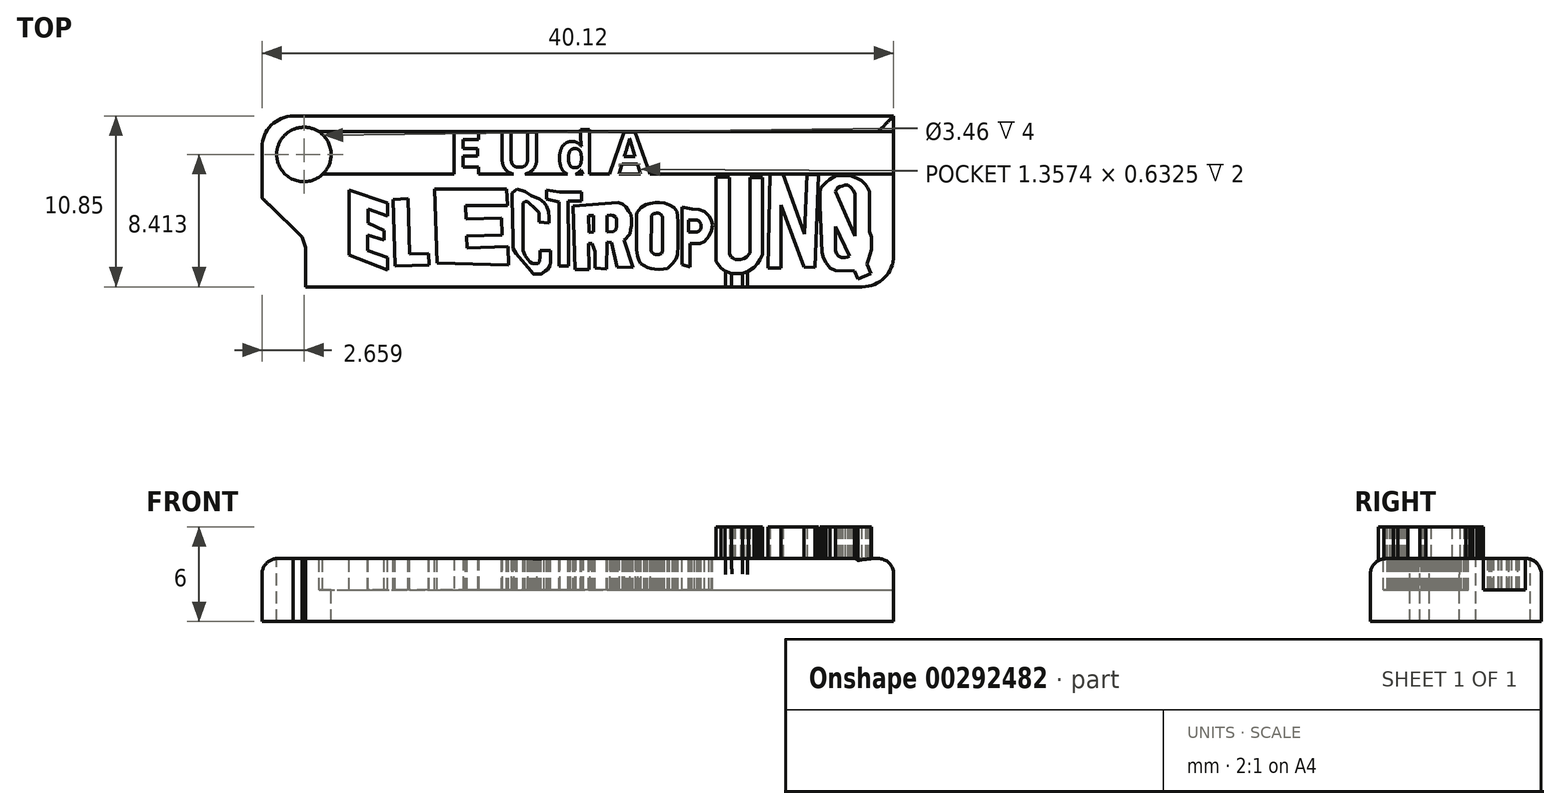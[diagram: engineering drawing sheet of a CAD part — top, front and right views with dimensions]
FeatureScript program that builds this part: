
annotation { "Feature Type Name" : "Feature", "Feature Type Description" : "" }
export const myFeature = defineFeature(function(context is Context, id is Id, definition is map)
    precondition{}
    {
        {
            var Q0;
            Q0=qCreatedBy(makeId("Top.planeOp"),FACE);
            var sketch = newSketch(context, id + "F0", { "sketchPlane" : qUnion([Q0])});
            skLineSegment(sketch, "E0.bottom", {"start": v(-20.57, 6.35) * mm, "end": v(19.55, 6.35) * mm});
            skLineSegment(sketch, "E0.top", {"start": v(-20.57, -4.5) * mm, "end": v(19.55, -4.5) * mm});
            skLineSegment(sketch, "E0.left", {"start": v(-20.57, 6.35) * mm, "end": v(-20.57, -4.5) * mm});
            skLineSegment(sketch, "E0.right", {"start": v(19.55, 6.35) * mm, "end": v(19.55, -4.5) * mm});
            skSolve(sketch);
        }
        {
            var Q0;
            Q0 = qSketchRegion(id + "F0", true);
            extrude(context, id + "F1", {"entities" : qUnion([Q0]), "oppositeDirection" : true, "depth" : 4 * mm});
        }
        {
            var Q0;
            Q0=makeQuery(id+"F1.opExtrude","CAP_FACE",FACE,{"disambiguationData":[OSD([sQuery(id+"F0.wireOp",EDGE,"E0.bottom"),sQuery(id+"F0.wireOp",EDGE,"E0.top"),sQuery(id+"F0.wireOp",EDGE,"E0.left"),sQuery(id+"F0.wireOp",EDGE,"E0.right")])],"isStart":true});
            var sketch = newSketch(context, id + "F2", { "sketchPlane" : qUnion([Q0])});
            skCircle(sketch, "E1", {"center": v(-17.91, 3.91) * mm, "radius": 1.73 * mm});
            skPoint(sketch, "E1.first.point", {"position": v(-19.2, 5.07) * mm});
            skPoint(sketch, "E1.second.point", {"position": v(-16.55, 2.84) * mm});
            skPoint(sketch, "E1.third.point", {"position": v(-16.4, 3.07) * mm});
            skSolve(sketch);
        }
        {
            var Q0;
            Q0=makeQuery(id+"F2.imprint","IMPRINT",FACE,{"disambiguationData":[TD([[makeQuery(id+"F2.imprint","IMPRINT",EDGE,{"derivedFrom":sQuery(id+"F2.wireOp",EDGE,"E1")}),1.0]])]});
            extrude(context, id + "F3", {"entities" : qUnion([Q0]), "operationType" : NewBodyOperationType.REMOVE, "oppositeDirection" : true, "depth" : 25 * mm});
        }
        {
            var Q0;
            Q0=qCreatedBy(makeId("Top.planeOp"),FACE);
            var sketch = newSketch(context, id + "F4", { "sketchPlane" : qUnion([Q0])});
            skLineSegment(sketch, "E2", {"start": v(-12.6, 0.81) * mm, "end": v(-12.6, 0) * mm});
            skLineSegment(sketch, "E3", {"start": v(-12.6, 0) * mm, "end": v(-13.83, 0.46) * mm});
            skLineSegment(sketch, "E4", {"start": v(-13.83, 0.46) * mm, "end": v(-13.83, -0.46) * mm});
            skLineSegment(sketch, "E5", {"start": v(-13.83, -0.46) * mm, "end": v(-12.8, -0.92) * mm});
            skLineSegment(sketch, "E6", {"start": v(-12.8, -0.92) * mm, "end": v(-12.8, -1.52) * mm});
            skLineSegment(sketch, "E7", {"start": v(-12.8, -1.52) * mm, "end": v(-13.87, -1.2) * mm});
            skLineSegment(sketch, "E8", {"start": v(-13.87, -1.2) * mm, "end": v(-13.87, -2.2) * mm});
            skLineSegment(sketch, "E9", {"start": v(-13.87, -2.2) * mm, "end": v(-12.6, -2.65) * mm});
            skLineSegment(sketch, "E10", {"start": v(-12.6, -2.65) * mm, "end": v(-12.6, -3.43) * mm});
            skLineSegment(sketch, "E11", {"start": v(-12.6, -3.43) * mm, "end": v(-15.03, -2.47) * mm});
            skLineSegment(sketch, "E12", {"start": v(-15.03, -2.47) * mm, "end": v(-15.03, 1.66) * mm});
            skLineSegment(sketch, "E13", {"start": v(-15.03, 1.66) * mm, "end": v(-12.6, 0.81) * mm});
            skLineSegment(sketch, "E14", {"start": v(-12.25, 1.06) * mm, "end": v(-12.1, -3.17) * mm});
            skLineSegment(sketch, "E15", {"start": v(-12.1, -3.17) * mm, "end": v(-9.96, -3.1) * mm});
            skLineSegment(sketch, "E16", {"start": v(-9.96, -3.1) * mm, "end": v(-9.99, -2.37) * mm});
            skLineSegment(sketch, "E17", {"start": v(-9.99, -2.37) * mm, "end": v(-11.19, -2.4) * mm});
            skLineSegment(sketch, "E18", {"start": v(-11.19, -2.4) * mm, "end": v(-11.3, 1.11) * mm});
            skLineSegment(sketch, "E19", {"start": v(-11.3, 1.11) * mm, "end": v(-12.25, 1.06) * mm});
            skLineSegment(sketch, "E20", {"start": v(-5, 0.65) * mm, "end": v(-5.03, 1.7) * mm});
            skLineSegment(sketch, "E21", {"start": v(-5.03, 1.7) * mm, "end": v(-9.6, 1.7) * mm});
            skLineSegment(sketch, "E22", {"start": v(-9.6, 1.7) * mm, "end": v(-9.45, -2.98) * mm});
            skLineSegment(sketch, "E23", {"start": v(-9.45, -2.98) * mm, "end": v(-4.91, -3.1) * mm});
            skLineSegment(sketch, "E24", {"start": v(-4.91, -3.1) * mm, "end": v(-4.95, -1.94) * mm});
            skLineSegment(sketch, "E25", {"start": v(-4.95, -1.94) * mm, "end": v(-7.54, -2.03) * mm});
            skLineSegment(sketch, "E26", {"start": v(-7.54, -2.03) * mm, "end": v(-7.56, -1.27) * mm});
            skLineSegment(sketch, "E27", {"start": v(-7.56, -1.27) * mm, "end": v(-5.32, -1.19) * mm});
            skLineSegment(sketch, "E28", {"start": v(-5.32, -1.19) * mm, "end": v(-5.36, -0.12) * mm});
            skLineSegment(sketch, "E29", {"start": v(-5.36, -0.12) * mm, "end": v(-7.6, -0.2) * mm});
            skLineSegment(sketch, "E30", {"start": v(-7.6, -0.2) * mm, "end": v(-7.63, 0.65) * mm});
            skLineSegment(sketch, "E31", {"start": v(-7.63, 0.65) * mm, "end": v(-5, 0.65) * mm});
            skLineSegment(sketch, "E32", {"start": v(-2.91, -2.17) * mm, "end": v(-2.24, -2.17) * mm});
            skLineSegment(sketch, "E33", {"start": v(-2.24, -2.17) * mm, "end": v(-2.24, -2.93) * mm});
            skLineSegment(sketch, "E34", {"start": v(-2.24, -2.93) * mm, "end": v(-2.28, -3.15) * mm});
            skLineSegment(sketch, "E35", {"start": v(-2.28, -3.15) * mm, "end": v(-2.44, -3.4) * mm});
            skLineSegment(sketch, "E36", {"start": v(-2.44, -3.4) * mm, "end": v(-2.84, -3.7) * mm});
            skLineSegment(sketch, "E37", {"start": v(-2.84, -3.7) * mm, "end": v(-2.95, -3.7) * mm});
            skLineSegment(sketch, "E38", {"start": v(-3.34, -3.7) * mm, "end": v(-2.95, -3.7) * mm});
            skLineSegment(sketch, "E39", {"start": v(-3.34, -3.7) * mm, "end": v(-4.43, -2.39) * mm});
            skLineSegment(sketch, "E40", {"start": v(-4.43, -2.39) * mm, "end": v(-4.63, -2.05) * mm});
            skLineSegment(sketch, "E41", {"start": v(-4.63, -2.05) * mm, "end": v(-4.63, -1.47) * mm});
            skLineSegment(sketch, "E42", {"start": v(-4.63, -1.47) * mm, "end": v(-4.7, 1.16) * mm});
            skLineSegment(sketch, "E43", {"start": v(-4.7, 1.16) * mm, "end": v(-4.7, 1.45) * mm});
            skLineSegment(sketch, "E44", {"start": v(-4.7, 1.45) * mm, "end": v(-4.38, 1.71) * mm});
            skLineSegment(sketch, "E45", {"start": v(-4.38, 1.71) * mm, "end": v(-3.87, 1.55) * mm});
            skLineSegment(sketch, "E46", {"start": v(-3.87, 1.55) * mm, "end": v(-3.5, 1.29) * mm});
            skLineSegment(sketch, "E47", {"start": v(-3.5, 1.29) * mm, "end": v(-2.95, 1.1) * mm});
            skLineSegment(sketch, "E48", {"start": v(-2.95, 1.1) * mm, "end": v(-2.65, 0.85) * mm});
            skLineSegment(sketch, "E49", {"start": v(-2.65, 0.85) * mm, "end": v(-2.49, 0.63) * mm});
            skLineSegment(sketch, "E50", {"start": v(-2.49, 0.63) * mm, "end": v(-2.36, 0.3) * mm});
            skLineSegment(sketch, "E51", {"start": v(-2.36, 0.3) * mm, "end": v(-2.33, -0.1) * mm});
            skLineSegment(sketch, "E52", {"start": v(-2.33, -0.1) * mm, "end": v(-2.33, -0.44) * mm});
            skLineSegment(sketch, "E53", {"start": v(-2.33, -0.44) * mm, "end": v(-2.98, -0.37) * mm});
            skLineSegment(sketch, "E54", {"start": v(-2.98, -0.37) * mm, "end": v(-2.98, 0.21) * mm});
            skLineSegment(sketch, "E55", {"start": v(-2.98, 0.21) * mm, "end": v(-3.18, 0.42) * mm});
            skLineSegment(sketch, "E56", {"start": v(-3.18, 0.42) * mm, "end": v(-3.7, 0.92) * mm});
            skLineSegment(sketch, "E57", {"start": v(-3.7, 0.92) * mm, "end": v(-3.87, 0.92) * mm});
            skLineSegment(sketch, "E58", {"start": v(-3.87, 0.92) * mm, "end": v(-3.98, 0.83) * mm});
            skLineSegment(sketch, "E59", {"start": v(-3.98, 0.83) * mm, "end": v(-3.98, 0.56) * mm});
            skLineSegment(sketch, "E60", {"start": v(-3.98, 0.56) * mm, "end": v(-3.98, -0.87) * mm});
            skLineSegment(sketch, "E61", {"start": v(-3.98, -0.87) * mm, "end": v(-3.98, -1.91) * mm});
            skLineSegment(sketch, "E62", {"start": v(-3.98, -1.91) * mm, "end": v(-3.98, -2.17) * mm});
            skLineSegment(sketch, "E63", {"start": v(-3.98, -2.17) * mm, "end": v(-3.87, -2.5) * mm});
            skLineSegment(sketch, "E64", {"start": v(-3.87, -2.5) * mm, "end": v(-3.7, -2.73) * mm});
            skLineSegment(sketch, "E65", {"start": v(-3.7, -2.73) * mm, "end": v(-3.54, -2.91) * mm});
            skLineSegment(sketch, "E66", {"start": v(-3.54, -2.91) * mm, "end": v(-3.4, -3) * mm});
            skLineSegment(sketch, "E67", {"start": v(-3.4, -3) * mm, "end": v(-3.18, -3) * mm});
            skLineSegment(sketch, "E68", {"start": v(-3.18, -3) * mm, "end": v(-3.05, -3) * mm});
            skLineSegment(sketch, "E69", {"start": v(-3.05, -3) * mm, "end": v(-2.95, -2.88) * mm});
            skLineSegment(sketch, "E70", {"start": v(-2.95, -2.88) * mm, "end": v(-2.9, -2.58) * mm});
            skLineSegment(sketch, "E71", {"start": v(-2.9, -2.58) * mm, "end": v(-2.91, -2.17) * mm});
            skLineSegment(sketch, "E72", {"start": v(-2.5, 1.09) * mm, "end": v(-2.5, 1.64) * mm});
            skLineSegment(sketch, "E73", {"start": v(-2.5, 1.64) * mm, "end": v(-1.68, 1.51) * mm});
            skLineSegment(sketch, "E74", {"start": v(-1.68, 1.51) * mm, "end": v(-0.27, 1.51) * mm});
            skLineSegment(sketch, "E75", {"start": v(-0.27, 1.51) * mm, "end": v(-0.27, 0.96) * mm});
            skLineSegment(sketch, "E76", {"start": v(-0.27, 0.96) * mm, "end": v(-1.13, 0.96) * mm});
            skLineSegment(sketch, "E77", {"start": v(-1.13, 0.96) * mm, "end": v(-1.12, -1.93) * mm});
            skLineSegment(sketch, "E78", {"start": v(-1.12, -1.93) * mm, "end": v(-1.12, -3.19) * mm});
            skLineSegment(sketch, "E79", {"start": v(-1.12, -3.19) * mm, "end": v(-1.71, -3.19) * mm});
            skLineSegment(sketch, "E80", {"start": v(-1.71, -3.19) * mm, "end": v(-1.71, -1.63) * mm});
            skLineSegment(sketch, "E81", {"start": v(-1.71, -1.63) * mm, "end": v(-1.71, 0.9) * mm});
            skLineSegment(sketch, "E82", {"start": v(-1.71, 0.9) * mm, "end": v(-2.5, 1.09) * mm});
            skLineSegment(sketch, "E83", {"start": v(-0.7, -3.39) * mm, "end": v(-0.82, 0.63) * mm});
            skLineSegment(sketch, "E84", {"start": v(-0.82, 0.63) * mm, "end": v(2.04, 0.84) * mm});
            skLineSegment(sketch, "E85", {"start": v(2.04, 0.84) * mm, "end": v(2.33, 0.77) * mm});
            skLineSegment(sketch, "E86", {"start": v(2.33, 0.77) * mm, "end": v(2.54, 0.58) * mm});
            skLineSegment(sketch, "E87", {"start": v(2.54, 0.58) * mm, "end": v(2.72, 0.3) * mm});
            skLineSegment(sketch, "E88", {"start": v(2.72, 0.3) * mm, "end": v(2.87, 0.08) * mm});
            skLineSegment(sketch, "E89", {"start": v(2.87, 0.08) * mm, "end": v(2.9, -0.2) * mm});
            skLineSegment(sketch, "E90", {"start": v(2.9, -0.2) * mm, "end": v(2.9, -0.6) * mm});
            skLineSegment(sketch, "E91", {"start": v(2.9, -0.6) * mm, "end": v(2.84, -0.86) * mm});
            skLineSegment(sketch, "E92", {"start": v(2.84, -0.86) * mm, "end": v(2.8, -1.13) * mm});
            skLineSegment(sketch, "E93", {"start": v(2.8, -1.13) * mm, "end": v(2.67, -1.28) * mm});
            skLineSegment(sketch, "E94", {"start": v(2.67, -1.28) * mm, "end": v(2.56, -1.43) * mm});
            skLineSegment(sketch, "E95", {"start": v(2.56, -1.43) * mm, "end": v(2.43, -1.52) * mm});
            skLineSegment(sketch, "E96", {"start": v(2.43, -1.52) * mm, "end": v(3, -3.27) * mm});
            skLineSegment(sketch, "E97", {"start": v(3, -3.27) * mm, "end": v(1.98, -3.23) * mm});
            skLineSegment(sketch, "E98", {"start": v(1.98, -3.23) * mm, "end": v(1.62, -1.67) * mm});
            skLineSegment(sketch, "E99", {"start": v(1.62, -1.67) * mm, "end": v(1.35, -1.65) * mm});
            skLineSegment(sketch, "E100", {"start": v(1.35, -1.65) * mm, "end": v(1.33, -3.35) * mm});
            skLineSegment(sketch, "E101", {"start": v(1.33, -3.35) * mm, "end": v(0.6, -3.31) * mm});
            skLineSegment(sketch, "E102", {"start": v(0.6, -3.31) * mm, "end": v(0.57, -2.24) * mm});
            skLineSegment(sketch, "E103", {"start": v(0.57, -2.24) * mm, "end": v(0.38, -1.74) * mm});
            skLineSegment(sketch, "E104", {"start": v(0.38, -1.74) * mm, "end": v(0.17, -1.74) * mm});
            skLineSegment(sketch, "E105", {"start": v(0.17, -1.74) * mm, "end": v(0.2, -3.4) * mm});
            skLineSegment(sketch, "E106", {"start": v(0.2, -3.4) * mm, "end": v(-0.7, -3.39) * mm});
            skLineSegment(sketch, "E107", {"start": v(0.48, -1.02) * mm, "end": v(0.18, -1.03) * mm});
            skLineSegment(sketch, "E108", {"start": v(0.18, -1.03) * mm, "end": v(0.18, 0.04) * mm});
            skLineSegment(sketch, "E109", {"start": v(0.18, 0.04) * mm, "end": v(0.48, 0.04) * mm});
            skLineSegment(sketch, "E110", {"start": v(0.48, 0.04) * mm, "end": v(0.48, -1.02) * mm});
            skLineSegment(sketch, "E111", {"start": v(1.34, 0.04) * mm, "end": v(1.34, -1.02) * mm});
            skLineSegment(sketch, "E112", {"start": v(1.34, -1.02) * mm, "end": v(1.74, -1) * mm});
            skLineSegment(sketch, "E113", {"start": v(1.74, -1) * mm, "end": v(1.9, -0.85) * mm});
            skLineSegment(sketch, "E114", {"start": v(1.9, -0.85) * mm, "end": v(1.96, -0.64) * mm});
            skLineSegment(sketch, "E115", {"start": v(1.96, -0.64) * mm, "end": v(1.95, -0.38) * mm});
            skLineSegment(sketch, "E116", {"start": v(1.95, -0.38) * mm, "end": v(1.93, -0.2) * mm});
            skLineSegment(sketch, "E117", {"start": v(1.93, -0.2) * mm, "end": v(1.87, -0.05) * mm});
            skLineSegment(sketch, "E118", {"start": v(1.87, -0.05) * mm, "end": v(1.73, 0.03) * mm});
            skLineSegment(sketch, "E119", {"start": v(1.73, 0.03) * mm, "end": v(1.56, 0.05) * mm});
            skLineSegment(sketch, "E120", {"start": v(1.56, 0.05) * mm, "end": v(1.38, 0.04) * mm});
            skLineSegment(sketch, "E121", {"start": v(1.38, 0.04) * mm, "end": v(1.34, 0.04) * mm});
            skLineSegment(sketch, "E122", {"start": v(3.23, 0) * mm, "end": v(3.23, -2.14) * mm});
            skLineSegment(sketch, "E123", {"start": v(3.23, -2.14) * mm, "end": v(3.27, -2.55) * mm});
            skLineSegment(sketch, "E124", {"start": v(3.27, -2.55) * mm, "end": v(3.38, -2.81) * mm});
            skLineSegment(sketch, "E125", {"start": v(3.38, -2.81) * mm, "end": v(3.45, -3.02) * mm});
            skLineSegment(sketch, "E126", {"start": v(3.45, -3.02) * mm, "end": v(3.68, -3.15) * mm});
            skLineSegment(sketch, "E127", {"start": v(3.68, -3.15) * mm, "end": v(3.92, -3.28) * mm});
            skLineSegment(sketch, "E128", {"start": v(3.92, -3.28) * mm, "end": v(4.13, -3.32) * mm});
            skLineSegment(sketch, "E129", {"start": v(4.13, -3.32) * mm, "end": v(4.37, -3.36) * mm});
            skLineSegment(sketch, "E130", {"start": v(4.37, -3.36) * mm, "end": v(4.63, -3.4) * mm});
            skLineSegment(sketch, "E131", {"start": v(4.63, -3.4) * mm, "end": v(4.93, -3.36) * mm});
            skLineSegment(sketch, "E132", {"start": v(4.93, -3.36) * mm, "end": v(5.2, -3.32) * mm});
            skLineSegment(sketch, "E133", {"start": v(5.2, -3.32) * mm, "end": v(5.5, -3.02) * mm});
            skLineSegment(sketch, "E134", {"start": v(5.5, -3.02) * mm, "end": v(5.72, -2.74) * mm});
            skLineSegment(sketch, "E135", {"start": v(5.72, -2.74) * mm, "end": v(5.81, -2.44) * mm});
            skLineSegment(sketch, "E136", {"start": v(5.81, -2.44) * mm, "end": v(5.85, -1.86) * mm});
            skLineSegment(sketch, "E137", {"start": v(5.85, -1.86) * mm, "end": v(5.85, -1.13) * mm});
            skLineSegment(sketch, "E138", {"start": v(5.85, -1.13) * mm, "end": v(5.85, -0.38) * mm});
            skLineSegment(sketch, "E139", {"start": v(5.85, -0.38) * mm, "end": v(5.83, 0.01) * mm});
            skLineSegment(sketch, "E140", {"start": v(5.83, 0.01) * mm, "end": v(5.77, 0.3) * mm});
            skLineSegment(sketch, "E141", {"start": v(5.77, 0.3) * mm, "end": v(5.6, 0.53) * mm});
            skLineSegment(sketch, "E142", {"start": v(5.6, 0.53) * mm, "end": v(5.32, 0.7) * mm});
            skLineSegment(sketch, "E143", {"start": v(5.32, 0.7) * mm, "end": v(5, 0.82) * mm});
            skLineSegment(sketch, "E144", {"start": v(5, 0.82) * mm, "end": v(4.69, 0.85) * mm});
            skLineSegment(sketch, "E145", {"start": v(4.69, 0.85) * mm, "end": v(4.4, 0.85) * mm});
            skLineSegment(sketch, "E146", {"start": v(4.4, 0.85) * mm, "end": v(4.07, 0.8) * mm});
            skLineSegment(sketch, "E147", {"start": v(4.07, 0.8) * mm, "end": v(3.8, 0.72) * mm});
            skLineSegment(sketch, "E148", {"start": v(3.8, 0.72) * mm, "end": v(3.5, 0.55) * mm});
            skLineSegment(sketch, "E149", {"start": v(3.5, 0.55) * mm, "end": v(3.34, 0.35) * mm});
            skLineSegment(sketch, "E150", {"start": v(3.34, 0.35) * mm, "end": v(3.25, 0.22) * mm});
            skLineSegment(sketch, "E151", {"start": v(3.25, 0.22) * mm, "end": v(3.22, 0.1) * mm});
            skLineSegment(sketch, "E152", {"start": v(3.22, 0.1) * mm, "end": v(3.23, 0) * mm});
            skLineSegment(sketch, "E153", {"start": v(4.16, -0.04) * mm, "end": v(4.14, -2.2) * mm});
            skLineSegment(sketch, "E154", {"start": v(4.14, -2.2) * mm, "end": v(4.2, -2.3) * mm});
            skLineSegment(sketch, "E155", {"start": v(4.2, -2.3) * mm, "end": v(4.28, -2.37) * mm});
            skLineSegment(sketch, "E156", {"start": v(4.28, -2.37) * mm, "end": v(4.34, -2.42) * mm});
            skLineSegment(sketch, "E157", {"start": v(4.34, -2.42) * mm, "end": v(4.43, -2.43) * mm});
            skLineSegment(sketch, "E158", {"start": v(4.43, -2.43) * mm, "end": v(4.53, -2.45) * mm});
            skLineSegment(sketch, "E159", {"start": v(4.53, -2.45) * mm, "end": v(4.64, -2.44) * mm});
            skLineSegment(sketch, "E160", {"start": v(4.64, -2.44) * mm, "end": v(4.71, -2.42) * mm});
            skLineSegment(sketch, "E161", {"start": v(4.71, -2.42) * mm, "end": v(4.8, -2.38) * mm});
            skLineSegment(sketch, "E162", {"start": v(4.8, -2.38) * mm, "end": v(4.84, -2.3) * mm});
            skLineSegment(sketch, "E163", {"start": v(4.84, -2.3) * mm, "end": v(4.87, -2.18) * mm});
            skLineSegment(sketch, "E164", {"start": v(4.87, -2.18) * mm, "end": v(4.87, -0.06) * mm});
            skLineSegment(sketch, "E165", {"start": v(4.87, -0.06) * mm, "end": v(4.84, 0.01) * mm});
            skLineSegment(sketch, "E166", {"start": v(4.84, 0.01) * mm, "end": v(4.78, 0.1) * mm});
            skLineSegment(sketch, "E167", {"start": v(4.78, 0.1) * mm, "end": v(4.67, 0.14) * mm});
            skLineSegment(sketch, "E168", {"start": v(4.67, 0.14) * mm, "end": v(4.57, 0.18) * mm});
            skLineSegment(sketch, "E169", {"start": v(4.57, 0.18) * mm, "end": v(4.47, 0.18) * mm});
            skLineSegment(sketch, "E170", {"start": v(4.47, 0.18) * mm, "end": v(4.39, 0.16) * mm});
            skLineSegment(sketch, "E171", {"start": v(4.39, 0.16) * mm, "end": v(4.3, 0.14) * mm});
            skLineSegment(sketch, "E172", {"start": v(4.3, 0.14) * mm, "end": v(4.22, 0.08) * mm});
            skLineSegment(sketch, "E173", {"start": v(4.22, 0.08) * mm, "end": v(4.16, 0.04) * mm});
            skLineSegment(sketch, "E174", {"start": v(4.16, 0.04) * mm, "end": v(4.16, -0.04) * mm});
            skLineSegment(sketch, "E175", {"start": v(6.12, 0.58) * mm, "end": v(6.12, -3.1) * mm});
            skLineSegment(sketch, "E176", {"start": v(6.12, -3.1) * mm, "end": v(6.61, -3.22) * mm});
            skLineSegment(sketch, "E177", {"start": v(6.61, -3.22) * mm, "end": v(6.61, -1.73) * mm});
            skLineSegment(sketch, "E178", {"start": v(6.61, -1.73) * mm, "end": v(7.25, -1.74) * mm});
            skLineSegment(sketch, "E179", {"start": v(7.25, -1.74) * mm, "end": v(7.53, -1.62) * mm});
            skLineSegment(sketch, "E180", {"start": v(7.53, -1.62) * mm, "end": v(7.83, -1.28) * mm});
            skLineSegment(sketch, "E181", {"start": v(7.83, -1.28) * mm, "end": v(7.98, -0.93) * mm});
            skLineSegment(sketch, "E182", {"start": v(7.98, -0.93) * mm, "end": v(8.04, -0.57) * mm});
            skLineSegment(sketch, "E183", {"start": v(8.04, -0.57) * mm, "end": v(7.98, -0.27) * mm});
            skLineSegment(sketch, "E184", {"start": v(7.98, -0.27) * mm, "end": v(7.82, 0) * mm});
            skLineSegment(sketch, "E185", {"start": v(7.82, 0) * mm, "end": v(7.53, 0.27) * mm});
            skLineSegment(sketch, "E186", {"start": v(7.53, 0.27) * mm, "end": v(7.18, 0.4) * mm});
            skLineSegment(sketch, "E187", {"start": v(7.18, 0.4) * mm, "end": v(6.74, 0.46) * mm});
            skLineSegment(sketch, "E188", {"start": v(6.74, 0.46) * mm, "end": v(6.12, 0.58) * mm});
            skLineSegment(sketch, "E189", {"start": v(6.53, -0.25) * mm, "end": v(6.53, -1) * mm});
            skLineSegment(sketch, "E190", {"start": v(6.53, -1) * mm, "end": v(7.07, -1.01) * mm});
            skLineSegment(sketch, "E191", {"start": v(7.07, -1.01) * mm, "end": v(7.18, -0.95) * mm});
            skLineSegment(sketch, "E192", {"start": v(7.18, -0.95) * mm, "end": v(7.28, -0.85) * mm});
            skLineSegment(sketch, "E193", {"start": v(7.28, -0.85) * mm, "end": v(7.3, -0.72) * mm});
            skLineSegment(sketch, "E194", {"start": v(7.3, -0.72) * mm, "end": v(7.32, -0.6) * mm});
            skLineSegment(sketch, "E195", {"start": v(7.32, -0.6) * mm, "end": v(7.3, -0.5) * mm});
            skLineSegment(sketch, "E196", {"start": v(7.3, -0.5) * mm, "end": v(7.25, -0.41) * mm});
            skLineSegment(sketch, "E197", {"start": v(7.25, -0.41) * mm, "end": v(7.17, -0.33) * mm});
            skLineSegment(sketch, "E198", {"start": v(7.17, -0.33) * mm, "end": v(7.06, -0.26) * mm});
            skLineSegment(sketch, "E199", {"start": v(7.06, -0.26) * mm, "end": v(6.91, -0.26) * mm});
            skLineSegment(sketch, "E200", {"start": v(6.91, -0.26) * mm, "end": v(6.53, -0.25) * mm});
            skSolve(sketch);
        }
        {
            var Q0;
            Q0=makeQuery(id+"F1.opExtrude","CAP_FACE",FACE,{"disambiguationData":[OSD([sQuery(id+"F0.wireOp",EDGE,"E0.bottom"),sQuery(id+"F0.wireOp",EDGE,"E0.top"),sQuery(id+"F0.wireOp",EDGE,"E0.left"),sQuery(id+"F0.wireOp",EDGE,"E0.right")])],"isStart":true});
            var sketch = newSketch(context, id + "F5", { "sketchPlane" : qUnion([Q0])});
            skLineSegment(sketch, "E201", {"start": v(8.25, 2.48) * mm, "end": v(8.25, -2.53) * mm});
            skLineSegment(sketch, "E202", {"start": v(8.25, -2.53) * mm, "end": v(8.25, -2.9) * mm});
            skLineSegment(sketch, "E203", {"start": v(8.25, -2.9) * mm, "end": v(8.57, -3.29) * mm});
            skLineSegment(sketch, "E204", {"start": v(8.57, -3.29) * mm, "end": v(8.83, -3.48) * mm});
            skLineSegment(sketch, "E205", {"start": v(8.83, -3.48) * mm, "end": v(9.25, -3.64) * mm});
            skLineSegment(sketch, "E206", {"start": v(9.25, -3.64) * mm, "end": v(9.58, -3.64) * mm});
            skLineSegment(sketch, "E207", {"start": v(9.58, -3.64) * mm, "end": v(9.96, -3.64) * mm});
            skLineSegment(sketch, "E208", {"start": v(9.96, -3.64) * mm, "end": v(10.32, -3.48) * mm});
            skLineSegment(sketch, "E209", {"start": v(10.32, -3.48) * mm, "end": v(10.67, -3.27) * mm});
            skLineSegment(sketch, "E210", {"start": v(10.67, -3.27) * mm, "end": v(10.9, -3.03) * mm});
            skLineSegment(sketch, "E211", {"start": v(10.9, -3.03) * mm, "end": v(11.07, -2.75) * mm});
            skLineSegment(sketch, "E212", {"start": v(11.07, -2.75) * mm, "end": v(11.2, -2.45) * mm});
            skLineSegment(sketch, "E213", {"start": v(11.2, -2.45) * mm, "end": v(11.2, 2.44) * mm});
            skLineSegment(sketch, "E214", {"start": v(11.2, 2.44) * mm, "end": v(10.44, 2.44) * mm});
            skLineSegment(sketch, "E215", {"start": v(10.44, 2.44) * mm, "end": v(10.44, -2.08) * mm});
            skLineSegment(sketch, "E216", {"start": v(10.44, -2.08) * mm, "end": v(10.44, -2.33) * mm});
            skLineSegment(sketch, "E217", {"start": v(10.44, -2.33) * mm, "end": v(10.2, -2.6) * mm});
            skLineSegment(sketch, "E218", {"start": v(10.2, -2.6) * mm, "end": v(10.05, -2.7) * mm});
            skLineSegment(sketch, "E219", {"start": v(10.05, -2.7) * mm, "end": v(9.84, -2.75) * mm});
            skLineSegment(sketch, "E220", {"start": v(9.84, -2.75) * mm, "end": v(9.66, -2.75) * mm});
            skLineSegment(sketch, "E221", {"start": v(9.66, -2.75) * mm, "end": v(9.47, -2.75) * mm});
            skLineSegment(sketch, "E222", {"start": v(9.47, -2.75) * mm, "end": v(9.33, -2.68) * mm});
            skLineSegment(sketch, "E223", {"start": v(9.33, -2.68) * mm, "end": v(9.22, -2.6) * mm});
            skLineSegment(sketch, "E224", {"start": v(9.22, -2.6) * mm, "end": v(9.11, -2.4) * mm});
            skLineSegment(sketch, "E225", {"start": v(9.11, -2.4) * mm, "end": v(9.11, 2.43) * mm});
            skLineSegment(sketch, "E226", {"start": v(9.11, 2.43) * mm, "end": v(8.25, 2.48) * mm});
            skLineSegment(sketch, "E227", {"start": v(11.57, -3.31) * mm, "end": v(11.7, 2.68) * mm});
            skLineSegment(sketch, "E228", {"start": v(11.7, 2.68) * mm, "end": v(12.51, 2.66) * mm});
            skLineSegment(sketch, "E229", {"start": v(12.51, 2.66) * mm, "end": v(13.9, -1.15) * mm});
            skLineSegment(sketch, "E230", {"start": v(13.9, -1.15) * mm, "end": v(14.03, 2.63) * mm});
            skLineSegment(sketch, "E231", {"start": v(14.03, 2.63) * mm, "end": v(14.77, 2.6) * mm});
            skLineSegment(sketch, "E232", {"start": v(14.77, 2.6) * mm, "end": v(14.55, -3.27) * mm});
            skLineSegment(sketch, "E233", {"start": v(14.55, -3.27) * mm, "end": v(13.84, -3.25) * mm});
            skLineSegment(sketch, "E234", {"start": v(13.84, -3.25) * mm, "end": v(12.39, 0.68) * mm});
            skLineSegment(sketch, "E235", {"start": v(12.39, 0.68) * mm, "end": v(12.39, -3.3) * mm});
            skLineSegment(sketch, "E236", {"start": v(12.39, -3.3) * mm, "end": v(11.57, -3.31) * mm});
            skLineSegment(sketch, "E237", {"start": v(14.93, 1.8) * mm, "end": v(14.88, 1.57) * mm});
            skLineSegment(sketch, "E238", {"start": v(14.88, 1.57) * mm, "end": v(14.88, 1.08) * mm});
            skLineSegment(sketch, "E239", {"start": v(14.88, 1.08) * mm, "end": v(14.88, 0.67) * mm});
            skLineSegment(sketch, "E240", {"start": v(14.88, 0.67) * mm, "end": v(14.98, -2.32) * mm});
            skLineSegment(sketch, "E241", {"start": v(14.98, -2.32) * mm, "end": v(15.1, -2.68) * mm});
            skLineSegment(sketch, "E242", {"start": v(15.1, -2.68) * mm, "end": v(15.24, -2.95) * mm});
            skLineSegment(sketch, "E243", {"start": v(15.24, -2.95) * mm, "end": v(15.51, -3.31) * mm});
            skLineSegment(sketch, "E244", {"start": v(15.51, -3.31) * mm, "end": v(15.84, -3.46) * mm});
            skLineSegment(sketch, "E245", {"start": v(15.84, -3.46) * mm, "end": v(16.34, -3.47) * mm});
            skLineSegment(sketch, "E246", {"start": v(16.34, -3.47) * mm, "end": v(17.06, -3.5) * mm});
            skLineSegment(sketch, "E247", {"start": v(17.06, -3.5) * mm, "end": v(17.27, -4) * mm});
            skLineSegment(sketch, "E248", {"start": v(17.27, -4) * mm, "end": v(18.1, -3.66) * mm});
            skLineSegment(sketch, "E249", {"start": v(18.1, -3.66) * mm, "end": v(17.85, -3.04) * mm});
            skLineSegment(sketch, "E250", {"start": v(17.85, -3.04) * mm, "end": v(17.94, -2.75) * mm});
            skLineSegment(sketch, "E251", {"start": v(17.94, -2.75) * mm, "end": v(18.13, -2.12) * mm});
            skLineSegment(sketch, "E252", {"start": v(18.13, -2.12) * mm, "end": v(18.13, -1.35) * mm});
            skLineSegment(sketch, "E253", {"start": v(18.13, -1.35) * mm, "end": v(18.01, -1) * mm});
            skLineSegment(sketch, "E254", {"start": v(18.01, -1) * mm, "end": v(18.01, 1.21) * mm});
            skLineSegment(sketch, "E255", {"start": v(18.01, 1.21) * mm, "end": v(18.01, 1.57) * mm});
            skLineSegment(sketch, "E256", {"start": v(18.01, 1.57) * mm, "end": v(17.9, 1.81) * mm});
            skLineSegment(sketch, "E257", {"start": v(17.9, 1.81) * mm, "end": v(17.75, 2) * mm});
            skLineSegment(sketch, "E258", {"start": v(17.75, 2) * mm, "end": v(17.5, 2.24) * mm});
            skLineSegment(sketch, "E259", {"start": v(17.5, 2.24) * mm, "end": v(17.18, 2.43) * mm});
            skLineSegment(sketch, "E260", {"start": v(17.18, 2.43) * mm, "end": v(16.78, 2.56) * mm});
            skLineSegment(sketch, "E261", {"start": v(16.78, 2.56) * mm, "end": v(16.45, 2.56) * mm});
            skLineSegment(sketch, "E262", {"start": v(16.45, 2.56) * mm, "end": v(15.9, 2.56) * mm});
            skLineSegment(sketch, "E263", {"start": v(15.9, 2.56) * mm, "end": v(15.46, 2.33) * mm});
            skLineSegment(sketch, "E264", {"start": v(15.46, 2.33) * mm, "end": v(15.24, 2.12) * mm});
            skLineSegment(sketch, "E265", {"start": v(15.24, 2.12) * mm, "end": v(14.93, 1.8) * mm});
            skLineSegment(sketch, "E266", {"start": v(17.1, -1.27) * mm, "end": v(15.84, 1.55) * mm});
            skLineSegment(sketch, "E267", {"start": v(15.84, 1.55) * mm, "end": v(15.9, 1.68) * mm});
            skLineSegment(sketch, "E268", {"start": v(15.9, 1.68) * mm, "end": v(15.98, 1.79) * mm});
            skLineSegment(sketch, "E269", {"start": v(15.98, 1.79) * mm, "end": v(16.13, 1.87) * mm});
            skLineSegment(sketch, "E270", {"start": v(16.13, 1.87) * mm, "end": v(16.3, 1.9) * mm});
            skLineSegment(sketch, "E271", {"start": v(16.3, 1.9) * mm, "end": v(16.44, 1.97) * mm});
            skLineSegment(sketch, "E272", {"start": v(16.44, 1.97) * mm, "end": v(16.64, 1.97) * mm});
            skLineSegment(sketch, "E273", {"start": v(16.64, 1.97) * mm, "end": v(16.84, 1.81) * mm});
            skLineSegment(sketch, "E274", {"start": v(16.84, 1.81) * mm, "end": v(16.98, 1.64) * mm});
            skLineSegment(sketch, "E275", {"start": v(16.98, 1.64) * mm, "end": v(17.08, 1.44) * mm});
            skLineSegment(sketch, "E276", {"start": v(17.08, 1.44) * mm, "end": v(17.1, 1.18) * mm});
            skLineSegment(sketch, "E277", {"start": v(17.1, 1.18) * mm, "end": v(17.1, -1.27) * mm});
            skLineSegment(sketch, "E278", {"start": v(15.84, -0.67) * mm, "end": v(15.84, -2.2) * mm});
            skLineSegment(sketch, "E279", {"start": v(15.84, -2.2) * mm, "end": v(15.9, -2.38) * mm});
            skLineSegment(sketch, "E280", {"start": v(15.9, -2.38) * mm, "end": v(16.04, -2.55) * mm});
            skLineSegment(sketch, "E281", {"start": v(16.04, -2.55) * mm, "end": v(16.22, -2.63) * mm});
            skLineSegment(sketch, "E282", {"start": v(16.22, -2.63) * mm, "end": v(16.44, -2.63) * mm});
            skLineSegment(sketch, "E283", {"start": v(16.44, -2.63) * mm, "end": v(16.62, -2.6) * mm});
            skLineSegment(sketch, "E284", {"start": v(16.62, -2.6) * mm, "end": v(16.75, -2.54) * mm});
            skLineSegment(sketch, "E285", {"start": v(16.75, -2.54) * mm, "end": v(15.84, -0.67) * mm});
            skSolve(sketch);
        }
        {
            var Q0;
            Q0=makeQuery(id+"F1.opExtrude","SWEPT_EDGE",EDGE,{"disambiguationData":[OSD([sQuery(id+"F0.wireOp",EDGE,"E0.bottom"),sQuery(id+"F0.wireOp",EDGE,"E0.left")])]});
            fillet(context, id + "F6", {"entities" : qUnion([Q0]), "radius" : 2 * mm, "tangentPropagation" : true, "allowEdgeOverflow" : false});
        }
        {
            var Q0;
            Q0=makeQuery(id+"F1.opExtrude","SWEPT_EDGE",EDGE,{"disambiguationData":[OSD([sQuery(id+"F0.wireOp",EDGE,"E0.top"),sQuery(id+"F0.wireOp",EDGE,"E0.right")])]});
            fillet(context, id + "F7", {"entities" : qUnion([Q0]), "radius" : 2 * mm, "tangentPropagation" : true, "allowEdgeOverflow" : false});
        }
        {
            var Q0;
            Q0 = qSketchRegion(id + "F4", true);
            extrude(context, id + "F8", {"entities" : qUnion([Q0]), "operationType" : NewBodyOperationType.REMOVE, "oppositeDirection" : true, "depth" : 2 * mm});
        }
        {
            var Q0;
            Q0 = qSketchRegion(id + "F5", true);
            extrude(context, id + "F9", {"entities" : qUnion([Q0]), "operationType" : NewBodyOperationType.ADD, "depth" : 2 * mm});
        }
        {
            var Q0;
            {var subQ62=sQuery(id+"F0.wireOp",EDGE,"E0.right");var subQ77=sQuery(id+"F0.wireOp",EDGE,"E0.top");var subQ83=sQuery(id+"F0.wireOp",EDGE,"E0.left");var subQ91=sQuery(id+"F0.wireOp",EDGE,"E0.bottom");var subQ149=makeQuery(id+"F1.opExtrude","SWEPT_FACE",FACE,{"disambiguationData":[OSD([subQ91])]});Q0=makeQuery(id+"F9.boolean.opBoolean","SPLIT",FACE,{"disambiguationData":[TD([subQ149])],"derivedFrom":makeQuery(id+"F8.boolean.opBoolean","SPLIT",FACE,{"disambiguationData":[TD([subQ149])],"derivedFrom":makeQuery(id+"F1.opExtrude","CAP_FACE",FACE,{"disambiguationData":[OSD([subQ91,subQ77,subQ83,subQ62])],"isStart":true})})});}
            var sketch = newSketch(context, id + "F10", { "sketchPlane" : qUnion([Q0])});
            skLineSegment(sketch, "E286", {"start": v(-20.57, 1.15) * mm, "end": v(-18.59, -0.77) * mm});
            skLineSegment(sketch, "E287", {"start": v(-18.59, -0.77) * mm, "end": v(-18.04, -1.35) * mm});
            skLineSegment(sketch, "E288", {"start": v(-18.04, -1.35) * mm, "end": v(-17.81, -2) * mm});
            skLineSegment(sketch, "E289", {"start": v(-17.81, -2) * mm, "end": v(-17.81, -2.9) * mm});
            skLineSegment(sketch, "E290", {"start": v(-17.81, -2.9) * mm, "end": v(-17.81, -4.5) * mm});
            skLineSegment(sketch, "E291", {"start": v(-17.81, -4.5) * mm, "end": v(-18.16, -5.54) * mm});
            skLineSegment(sketch, "E292", {"start": v(-18.16, -5.54) * mm, "end": v(-21.78, -4.12) * mm});
            skLineSegment(sketch, "E293", {"start": v(-21.78, -4.12) * mm, "end": v(-21.3, 0.65) * mm});
            skLineSegment(sketch, "E294", {"start": v(-21.3, 0.65) * mm, "end": v(-20.57, 1.15) * mm});
            skSolve(sketch);
        }
        {
            var Q0;
            Q0 = qSketchRegion(id + "F10", true);
            extrude(context, id + "F11", {"entities" : qUnion([Q0]), "operationType" : NewBodyOperationType.REMOVE, "oppositeDirection" : true, "depth" : 25 * mm});
        }
        {
            var Q0;
            Q0=makeQuery(id+"F1.opExtrude","CAP_EDGE",EDGE,{"disambiguationData":[OSD([sQuery(id+"F0.wireOp",EDGE,"E0.bottom")])],"isStart":true});
            var Q1;
            {var subQ0=sQuery(id+"F0.wireOp",EDGE,"E0.left");var subQ1=sQuery(id+"F0.wireOp",EDGE,"E0.bottom");Q1=makeQuery(id+"F6.opFillet","BLEND_EDGE",EDGE,{"blendedFrom":[makeQuery(id+"F1.opExtrude","SWEPT_EDGE",EDGE,{"disambiguationData":[OSD([subQ1,subQ0])]}),makeQuery(id+"F1.opExtrude","CAP_FACE",FACE,{"disambiguationData":[OSD([subQ1,sQuery(id+"F0.wireOp",EDGE,"E0.top"),subQ0,sQuery(id+"F0.wireOp",EDGE,"E0.right")])],"isStart":true})],"blendedInto":[makeQuery(id+"F1.opExtrude","CAP_FACE",FACE,{"disambiguationData":[OSD([subQ1,sQuery(id+"F0.wireOp",EDGE,"E0.top"),subQ0,sQuery(id+"F0.wireOp",EDGE,"E0.right")])],"isStart":true})]});}
            var Q2;
            Q2=makeQuery(id+"F1.opExtrude","CAP_EDGE",EDGE,{"disambiguationData":[OSD([sQuery(id+"F0.wireOp",EDGE,"E0.left")])],"isStart":true});
            var Q3;
            Q3=makeQuery(id+"F11.boolean.opBoolean","COPY",EDGE,{"derivedFrom":makeQuery(id+"F11.opExtrude","CAP_EDGE",EDGE,{"disambiguationData":[OSD([sQuery(id+"F10.wireOp",EDGE,"E286")])],"isStart":true})});
            var Q4;
            Q4=makeQuery(id+"F11.boolean.opBoolean","COPY",EDGE,{"derivedFrom":makeQuery(id+"F11.opExtrude","CAP_EDGE",EDGE,{"disambiguationData":[OSD([sQuery(id+"F10.wireOp",EDGE,"E287")])],"isStart":true})});
            var Q5;
            Q5=makeQuery(id+"F11.boolean.opBoolean","COPY",EDGE,{"derivedFrom":makeQuery(id+"F11.opExtrude","CAP_EDGE",EDGE,{"disambiguationData":[OSD([sQuery(id+"F10.wireOp",EDGE,"E288")])],"isStart":true})});
            var Q6;
            Q6=makeQuery(id+"F11.boolean.opBoolean","COPY",EDGE,{"derivedFrom":makeQuery(id+"F11.opExtrude","CAP_EDGE",EDGE,{"disambiguationData":[OSD([sQuery(id+"F10.wireOp",EDGE,"E289"),sQuery(id+"F10.wireOp",EDGE,"E290")])],"isStart":true})});
            var Q7;
            Q7=makeQuery(id+"F1.opExtrude","CAP_EDGE",EDGE,{"disambiguationData":[OSD([sQuery(id+"F0.wireOp",EDGE,"E0.top")])],"isStart":true});
            var Q8;
            {var subQ0=sQuery(id+"F0.wireOp",EDGE,"E0.right");var subQ1=sQuery(id+"F0.wireOp",EDGE,"E0.top");Q8=makeQuery(id+"F7.opFillet","BLEND_EDGE",EDGE,{"blendedFrom":[makeQuery(id+"F1.opExtrude","SWEPT_EDGE",EDGE,{"disambiguationData":[OSD([subQ1,subQ0])]}),makeQuery(id+"F1.opExtrude","CAP_FACE",FACE,{"disambiguationData":[OSD([sQuery(id+"F0.wireOp",EDGE,"E0.bottom"),subQ1,sQuery(id+"F0.wireOp",EDGE,"E0.left"),subQ0])],"isStart":true})],"blendedInto":[makeQuery(id+"F1.opExtrude","CAP_FACE",FACE,{"disambiguationData":[OSD([sQuery(id+"F0.wireOp",EDGE,"E0.bottom"),subQ1,sQuery(id+"F0.wireOp",EDGE,"E0.left"),subQ0])],"isStart":true})]});}
            var Q9;
            Q9=makeQuery(id+"F1.opExtrude","CAP_EDGE",EDGE,{"disambiguationData":[OSD([sQuery(id+"F0.wireOp",EDGE,"E0.right")])],"isStart":true});
            fillet(context, id + "F12", {"entities" : qUnion([Q0, Q1, Q2, Q3, Q4, Q5, Q6, Q7, Q8, Q9]), "radius" : 1 * mm, "tangentPropagation" : true, "allowEdgeOverflow" : false});
        }
        {
            var Q0;
            {var subQ62=sQuery(id+"F0.wireOp",EDGE,"E0.right");var subQ77=sQuery(id+"F0.wireOp",EDGE,"E0.top");var subQ83=sQuery(id+"F0.wireOp",EDGE,"E0.left");var subQ91=sQuery(id+"F0.wireOp",EDGE,"E0.bottom");var subQ149=makeQuery(id+"F1.opExtrude","SWEPT_FACE",FACE,{"disambiguationData":[OSD([subQ91])]});Q0=makeQuery(id+"F12.opFillet","SPLIT",FACE,{"disambiguationData":[OD(1.0)],"derivedFrom":makeQuery(id+"F9.boolean.opBoolean","SPLIT",FACE,{"disambiguationData":[TD([subQ149])],"derivedFrom":makeQuery(id+"F8.boolean.opBoolean","SPLIT",FACE,{"disambiguationData":[TD([subQ149])],"derivedFrom":makeQuery(id+"F1.opExtrude","CAP_FACE",FACE,{"disambiguationData":[OSD([subQ91,subQ77,subQ83,subQ62])],"isStart":true})})})});}
            var sketch = newSketch(context, id + "F13", { "sketchPlane" : qUnion([Q0])});
            skLineSegment(sketch, "E295.bottom", {"start": v(-16.95, 5.35) * mm, "end": v(19.94, 5.35) * mm});
            skLineSegment(sketch, "E295.top", {"start": v(-16.95, 2.66) * mm, "end": v(19.94, 2.66) * mm});
            skLineSegment(sketch, "E295.left", {"start": v(-16.95, 5.35) * mm, "end": v(-16.95, 2.66) * mm});
            skLineSegment(sketch, "E295.right", {"start": v(19.94, 5.35) * mm, "end": v(19.94, 2.66) * mm});
            skSolve(sketch);
        }
        {
            var Q0;
            Q0 = qSketchRegion(id + "F13", true);
            extrude(context, id + "F14", {"entities" : qUnion([Q0]), "operationType" : NewBodyOperationType.REMOVE, "oppositeDirection" : true, "depth" : 2 * mm});
        }
        {
            var Q0;
            Q0=makeQuery(id+"F14.boolean.opBoolean","COPY",FACE,{"derivedFrom":makeQuery(id+"F14.opExtrude","CAP_FACE",FACE,{"disambiguationData":[OSD([sQuery(id+"F13.wireOp",EDGE,"E295.bottom"),sQuery(id+"F13.wireOp",EDGE,"E295.top"),sQuery(id+"F13.wireOp",EDGE,"E295.left"),sQuery(id+"F13.wireOp",EDGE,"E295.right")])],"isStart":false})});
            var sketch = newSketch(context, id + "F15", { "sketchPlane" : qUnion([Q0])});
            skText(sketch, "E296", { "text": "E U d A", "fontName": "OpenSans-Bold.ttf"});
            const initialGuessF15  = {"E296": [-0.0087, 0.00266, 1, 0, 0.00269]};
            skSetInitialGuess(sketch, initialGuessF15);
            skSolve(sketch);
        }
        {
            var Q0;
            Q0 = qSketchRegion(id + "F15", true);
            extrude(context, id + "F16", {"entities" : qUnion([Q0]), "operationType" : NewBodyOperationType.ADD, "depth" : 2 * mm});
        }
    });
